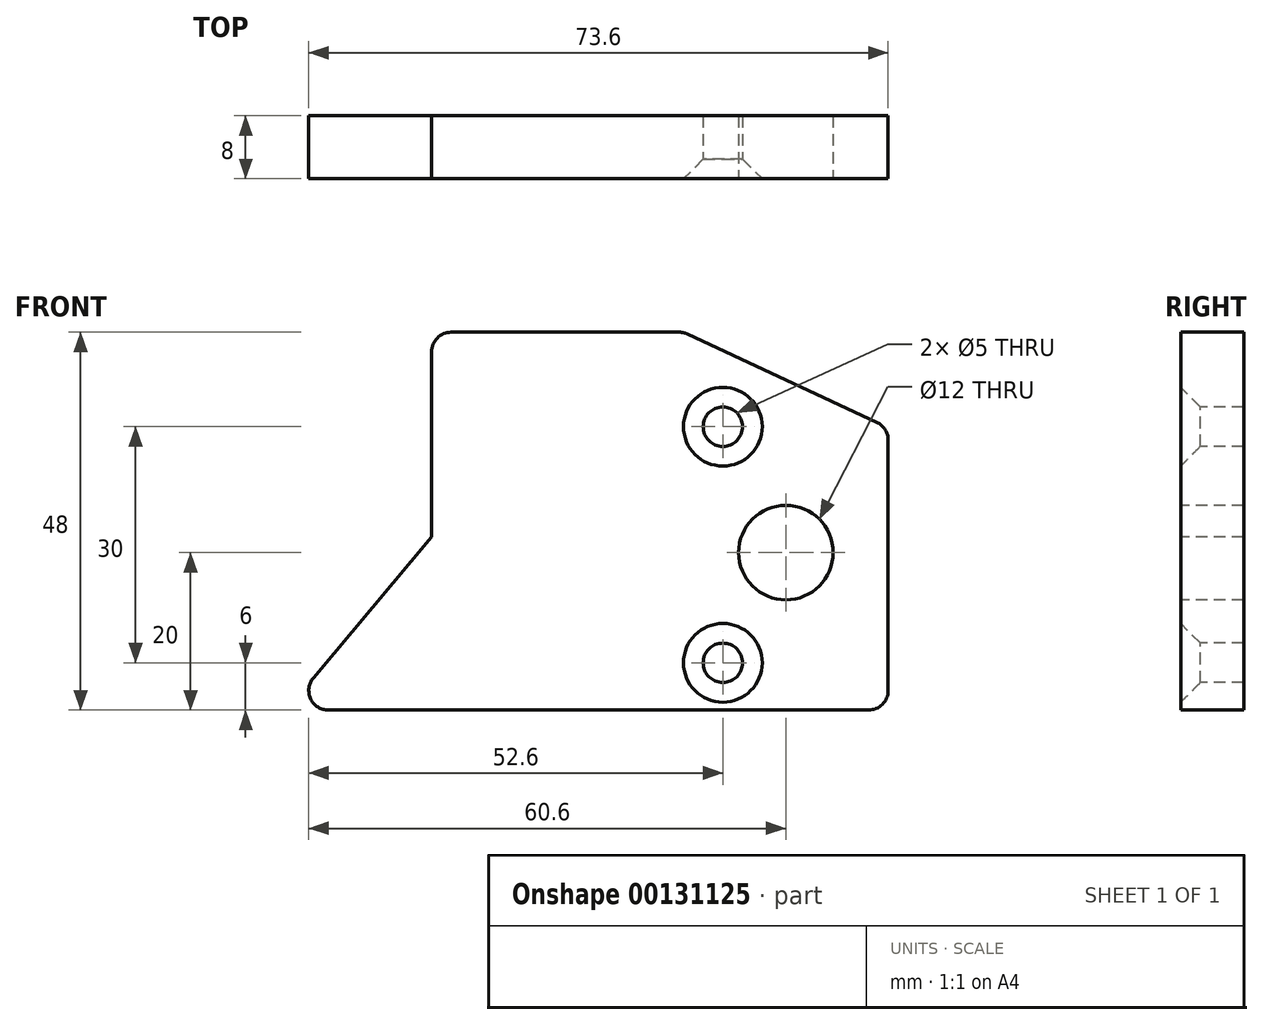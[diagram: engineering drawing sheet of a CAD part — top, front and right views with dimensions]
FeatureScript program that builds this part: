
annotation { "Feature Type Name" : "Feature", "Feature Type Description" : "" }
export const myFeature = defineFeature(function(context is Context, id is Id, definition is map)
    precondition{}
    {
        {
            var Q0;
            Q0=qCreatedBy(makeId("Front.planeOp"),FACE);
            var sketch = newSketch(context, id + "F0", { "sketchPlane" : qUnion([Q0])});
            skLineSegment(sketch, "E0.bottom", {"start": v(3, 24) * mm, "end": v(-29, 24) * mm});
            skLineSegment(sketch, "E0.top", {"start": v(29, -24) * mm, "end": v(3, -24) * mm});
            skLineSegment(sketch, "E0.left", {"start": v(29, 11.88) * mm, "end": v(29, -24) * mm});
            skLineSegment(sketch, "E0.right", {"start": v(-29, 24) * mm, "end": v(-29, -2) * mm});
            skPoint(sketch, "E0.middle", {"position": v(0, 0) * mm});
            skLineSegment(sketch, "E1", {"start": v(20, -24) * mm, "end": v(20, 24) * mm, "construction": true});
            skLineSegment(sketch, "E2", {"start": v(3, -24) * mm, "end": v(3, 24) * mm, "construction": true});
            skLineSegment(sketch, "E3", {"start": v(8, 24) * mm, "end": v(8, -24) * mm, "construction": true});
            skLineSegment(sketch, "E4", {"start": v(16, 24) * mm, "end": v(16, -24) * mm, "construction": true});
            skPoint(sketch, "E5", {"position": v(8, -18) * mm});
            skPoint(sketch, "E6", {"position": v(8, 12) * mm});
            skLineSegment(sketch, "E7", {"start": v(3, 24) * mm, "end": v(29, 11.88) * mm});
            skPoint(sketch, "E8.orphan", {"position": v(29, 24) * mm});
            skLineSegment(sketch, "E9", {"start": v(3, 24) * mm, "end": v(29, 24) * mm, "construction": true});
            skLineSegment(sketch, "E10", {"start": v(29, 11.88) * mm, "end": v(29, 24) * mm, "construction": true});
            skPoint(sketch, "E11", {"position": v(-29, -2) * mm});
            skLineSegment(sketch, "E12", {"start": v(-29, -2) * mm, "end": v(-47.46, -24) * mm});
            skPoint(sketch, "E13.orphan", {"position": v(-29, -24) * mm});
            skLineSegment(sketch, "E14", {"start": v(-47.46, -24) * mm, "end": v(3, -24) * mm});
            skPoint(sketch, "E15", {"position": v(20, 12) * mm});
            skPoint(sketch, "E16", {"position": v(16, -4) * mm});
            skSolve(sketch);
        }
        {
            var Q0;
            Q0=makeQuery(id+"F0.imprint","IMPRINT",FACE,{"disambiguationData":[TD([[makeQuery(id+"F0.imprint","IMPRINT",EDGE,{"derivedFrom":sQuery(id+"F0.wireOp",EDGE,"E0.bottom")}),1.0]])]});
            extrude(context, id + "F1", {"entities" : qUnion([Q0]), "oppositeDirection" : true, "depth" : 8 * mm});
        }
        {
            var Q0;
            Q0=sQuery(id+"F0.wireOp",VERTEX,"E5");
            var Q1;
            Q1=sQuery(id+"F0.wireOp",VERTEX,"E6");
            var Q2;
            Q2=makeQuery(id+"F1.opExtrude","SWEPT_BODY",BODY,{"disambiguationData":[OSD([sQuery(id+"F0.wireOp",EDGE,"E0.bottom"),sQuery(id+"F0.wireOp",EDGE,"E0.top"),sQuery(id+"F0.wireOp",EDGE,"E0.left"),sQuery(id+"F0.wireOp",EDGE,"E0.right"),sQuery(id+"F0.wireOp",EDGE,"E7"),sQuery(id+"F0.wireOp",EDGE,"E12"),sQuery(id+"F0.wireOp",EDGE,"E14")])]});
            hole(context, id + "F2", {"style" : HoleStyle.C_SINK, "endStyle" : HoleEndStyle.THROUGH, "holeDiameter" : 5 * mm, "cSinkDiameter" : 10 * mm, "cSinkAngle" : 90 * degree, "locations" : qUnion([Q0, Q1]), "scope" : qUnion([Q2]), "isTappedThrough" : true});
        }
        {
            var Q0;
            Q0=sQuery(id+"F0.wireOp",VERTEX,"E16");
            var Q1;
            Q1=makeQuery(id+"F1.opExtrude","SWEPT_BODY",BODY,{"disambiguationData":[OSD([sQuery(id+"F0.wireOp",EDGE,"E0.bottom"),sQuery(id+"F0.wireOp",EDGE,"E0.top"),sQuery(id+"F0.wireOp",EDGE,"E0.left"),sQuery(id+"F0.wireOp",EDGE,"E0.right"),sQuery(id+"F0.wireOp",EDGE,"E7"),sQuery(id+"F0.wireOp",EDGE,"E12"),sQuery(id+"F0.wireOp",EDGE,"E14")])]});
            hole(context, id + "F3", {"style" : HoleStyle.SIMPLE, "endStyle" : HoleEndStyle.THROUGH, "holeDiameter" : 12 * mm, "locations" : qUnion([Q0]), "scope" : qUnion([Q1]), "isTappedThrough" : true});
        }
        {
            var Q0;
            Q0=makeQuery(id+"F1.opExtrude","SWEPT_EDGE",EDGE,{"disambiguationData":[OSD([sQuery(id+"F0.wireOp",EDGE,"E12"),sQuery(id+"F0.wireOp",EDGE,"E14")])]});
            var Q1;
            Q1=makeQuery(id+"F1.opExtrude","SWEPT_EDGE",EDGE,{"disambiguationData":[OSD([sQuery(id+"F0.wireOp",EDGE,"E0.bottom"),sQuery(id+"F0.wireOp",EDGE,"E0.right")])]});
            var Q2;
            Q2=makeQuery(id+"F1.opExtrude","SWEPT_EDGE",EDGE,{"disambiguationData":[OSD([sQuery(id+"F0.wireOp",EDGE,"E0.bottom"),sQuery(id+"F0.wireOp",EDGE,"E7")])]});
            var Q3;
            Q3=makeQuery(id+"F1.opExtrude","SWEPT_EDGE",EDGE,{"disambiguationData":[OSD([sQuery(id+"F0.wireOp",EDGE,"E0.left"),sQuery(id+"F0.wireOp",EDGE,"E7")])]});
            var Q4;
            Q4=makeQuery(id+"F1.opExtrude","SWEPT_EDGE",EDGE,{"disambiguationData":[OSD([sQuery(id+"F0.wireOp",EDGE,"E0.top"),sQuery(id+"F0.wireOp",EDGE,"E0.left")])]});
            fillet(context, id + "F4", {"entities" : qUnion([Q0, Q1, Q2, Q3, Q4]), "radius" : 2.5 * mm, "tangentPropagation" : true, "allowEdgeOverflow" : false});
        }
    });
